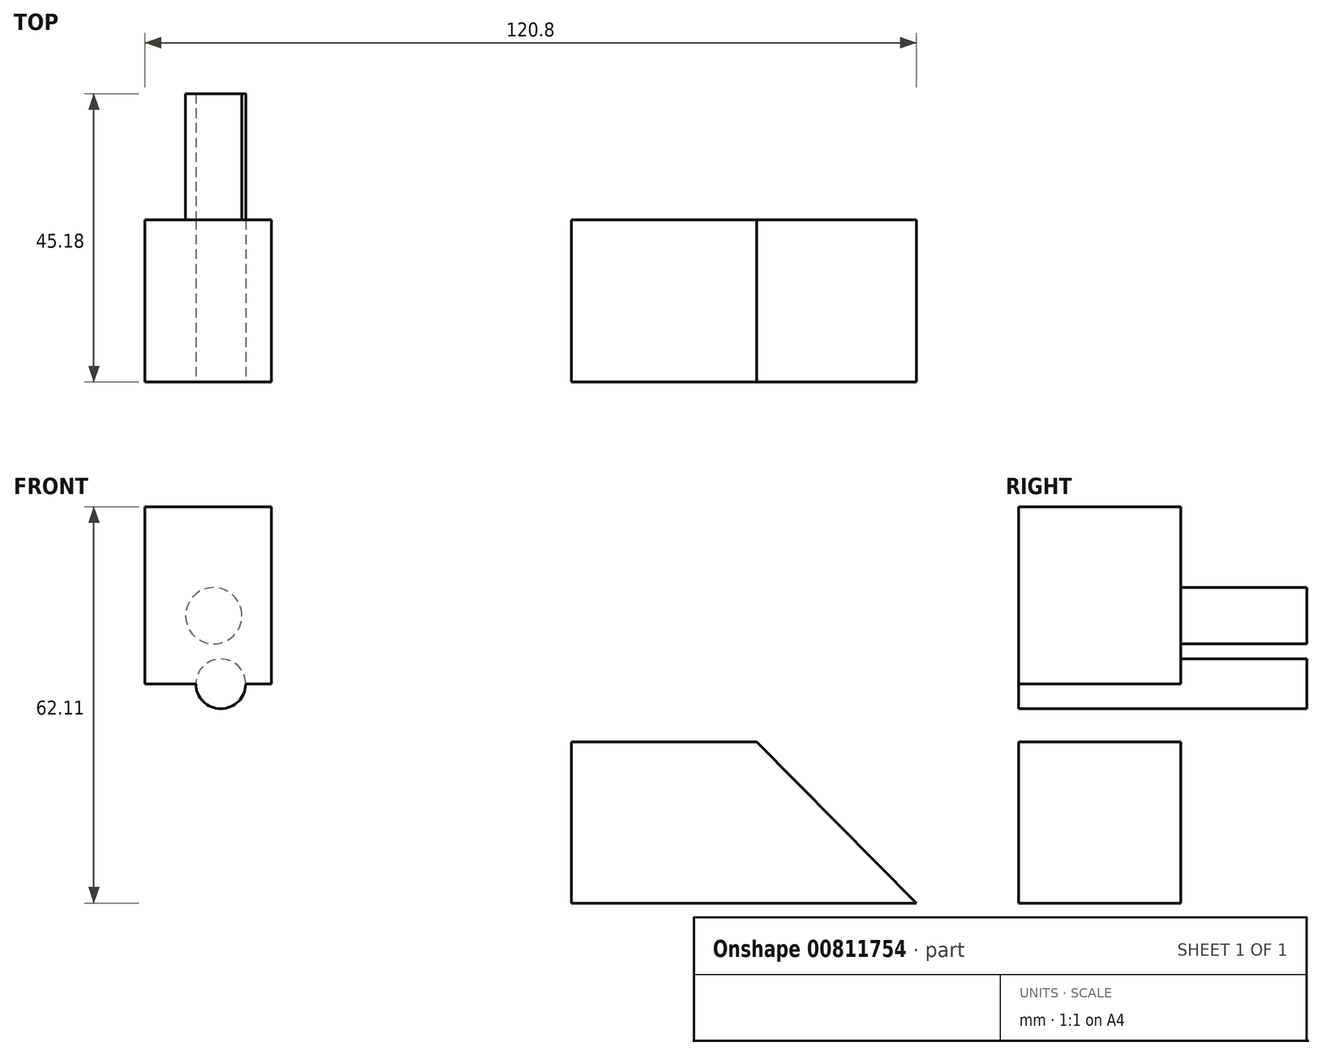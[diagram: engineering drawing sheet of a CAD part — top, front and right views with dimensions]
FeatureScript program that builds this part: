
annotation { "Feature Type Name" : "Feature", "Feature Type Description" : "" }
export const myFeature = defineFeature(function(context is Context, id is Id, definition is map)
    precondition{}
    {
        {
            var Q0;
            Q0=qCreatedBy(makeId("Front.planeOp"),FACE);
            var sketch = newSketch(context, id + "F0", { "sketchPlane" : qUnion([Q0])});
            skLineSegment(sketch, "E0.bottom", {"start": v(-66.79, 36.89) * mm, "end": v(-46.98, 36.89) * mm});
            skLineSegment(sketch, "E0.top", {"start": v(-66.79, 9.12) * mm, "end": v(-46.98, 9.12) * mm});
            skLineSegment(sketch, "E0.left", {"start": v(-66.79, 36.89) * mm, "end": v(-66.79, 9.12) * mm});
            skLineSegment(sketch, "E0.right", {"start": v(-46.98, 36.89) * mm, "end": v(-46.98, 9.12) * mm});
            skSolve(sketch);
        }
        {
            var Q0;
            Q0 = qSketchRegion(id + "F0", true);
            extrude(context, id + "F1", {"entities" : qUnion([Q0]), "depth" : 25.4 * mm, "offsetDistance" : 25.4 * mm});
        }
        {
            var Q0;
            Q0=makeQuery(id+"F1.opExtrude","CAP_FACE",FACE,{"disambiguationData":[OSD([sQuery(id+"F0.wireOp",EDGE,"E0.bottom"),sQuery(id+"F0.wireOp",EDGE,"E0.top"),sQuery(id+"F0.wireOp",EDGE,"E0.left"),sQuery(id+"F0.wireOp",EDGE,"E0.right")])],"isStart":false});
            var sketch = newSketch(context, id + "F2", { "sketchPlane" : qUnion([Q0])});
            skCircle(sketch, "E1", {"center": v(-56.03, 19.8) * mm, "radius": 4.4 * mm});
            skCircle(sketch, "E2", {"center": v(-54.93, 9.12) * mm, "radius": 3.9 * mm});
            skSolve(sketch);
        }
        {
            var Q0;
            Q0 = qSketchRegion(id + "F2", true);
            extrude(context, id + "F3", {"entities" : qUnion([Q0]), "operationType" : NewBodyOperationType.ADD, "endBound" : BoundingType.THROUGH_ALL, "oppositeDirection" : true, "depth" : 35.36 * mm, "offsetDistance" : 25.4 * mm});
        }
        {
            var Q0;
            Q0=qCreatedBy(makeId("Front.planeOp"),FACE);
            var sketch = newSketch(context, id + "F4", { "sketchPlane" : qUnion([Q0])});
            skLineSegment(sketch, "E3", {"start": v(29, 0) * mm, "end": v(54.01, -25.22) * mm});
            skLineSegment(sketch, "E4", {"start": v(0, -25.22) * mm, "end": v(0, 0) * mm});
            skLineSegment(sketch, "E5", {"start": v(0, 0) * mm, "end": v(29, 0) * mm});
            skLineSegment(sketch, "E6", {"start": v(0, -25.22) * mm, "end": v(54.01, -25.22) * mm});
            skSolve(sketch);
        }
        {
            var Q0;
            Q0=makeQuery(id+"F4.imprint","IMPRINT",FACE,{"disambiguationData":[TD([[makeQuery(id+"F4.imprint","IMPRINT",EDGE,{"derivedFrom":sQuery(id+"F4.wireOp",EDGE,"E3")}),-1.0]])]});
            var Q1;
            Q1=makeQuery(id+"F3.opExtrude","CAP_FACE",FACE,{"disambiguationData":[OSD([sQuery(id+"F2.wireOp",EDGE,"E1")])],"isStart":false});
            var Q2;
            Q2=makeQuery(id+"F3.opExtrude","CAP_FACE",FACE,{"disambiguationData":[OSD([sQuery(id+"F2.wireOp",EDGE,"E2")])],"isStart":false});
            extrude(context, id + "F5", {"entities" : qUnion([Q0, Q1, Q2]), "operationType" : NewBodyOperationType.ADD, "depth" : 25.4 * mm, "offsetDistance" : 25.4 * mm});
        }
    });
